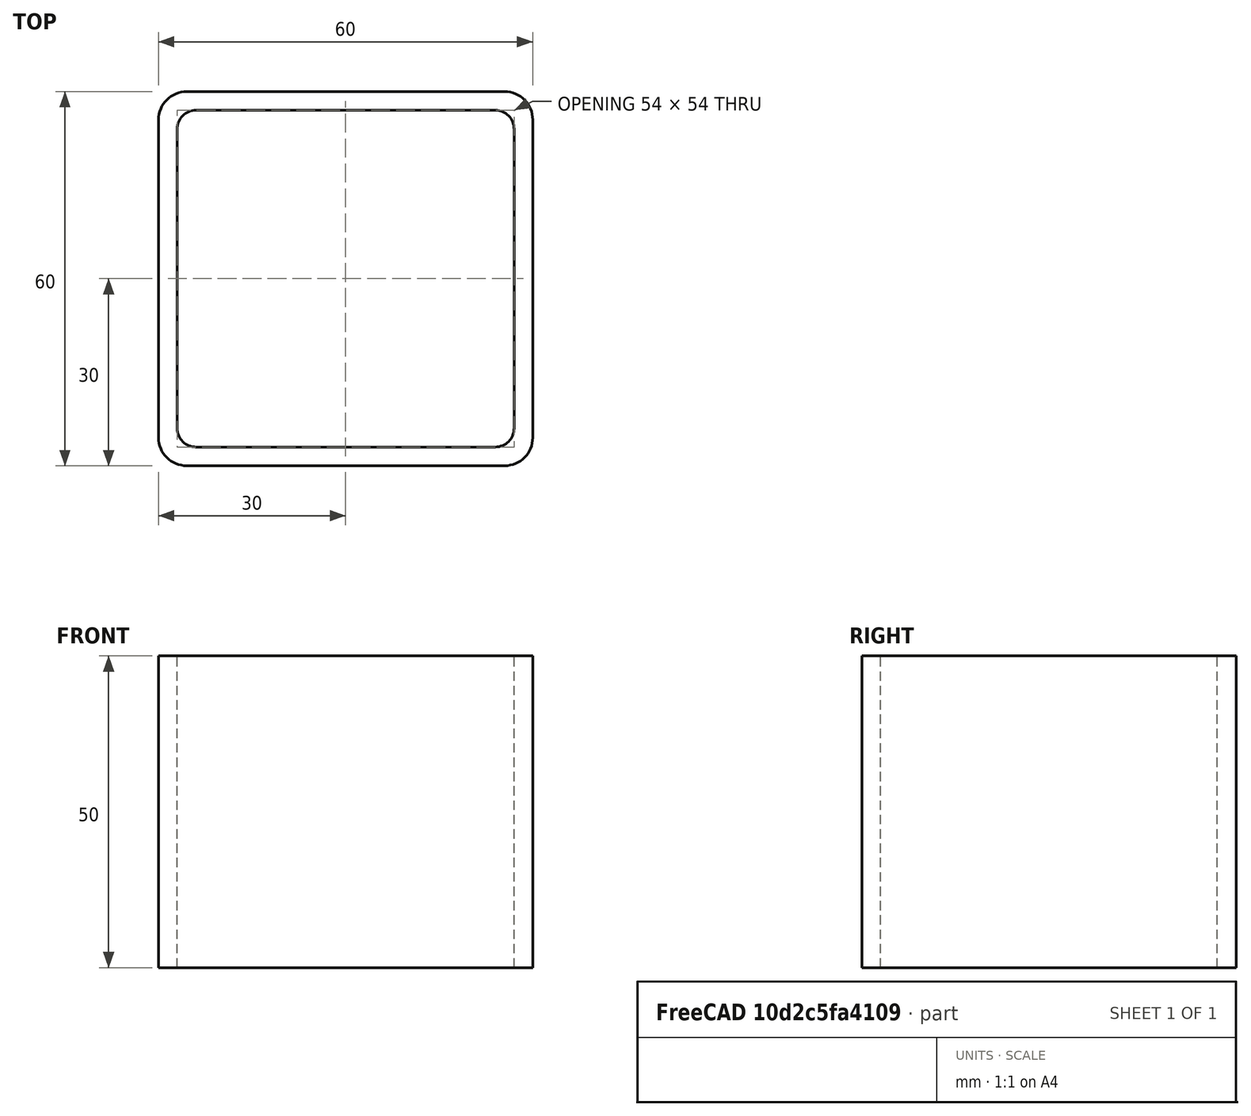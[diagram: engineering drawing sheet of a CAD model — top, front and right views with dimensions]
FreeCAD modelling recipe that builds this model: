
FCSTD DOCUMENT  (FreeCAD 0.15R4671 (Git))
Label: Square hollow section 60x60x3 EN10219 S235JRH
License: All rights reserved
LicenseURL: http://en.wikipedia.org/wiki/All_rights_reserved
objects: Sketcher::SketchObject×1, Part::Extrusion×1
note: 2 computed .brp shape members not serialized (recipe doc carries the construction recipe); baked Part::Feature solids carry a one-line shape summary decoded from their .brp

FEATURE [Sketcher::SketchObject] Sketch
  sketch-geometry (16):
    g0: LineSegment StartX=-24 StartY=27 StartZ=0 EndX=24 EndY=27 EndZ=0
    g1: LineSegment StartX=27 StartY=24 StartZ=0 EndX=27 EndY=-24 EndZ=0
    g2: LineSegment StartX=24 StartY=-27 StartZ=0 EndX=-24 EndY=-27 EndZ=0
    g3: LineSegment StartX=-27 StartY=-24 StartZ=0 EndX=-27 EndY=24 EndZ=0
    g4: LineSegment StartX=-25.5 StartY=30 StartZ=0 EndX=25.5 EndY=30 EndZ=0
    g5: LineSegment StartX=30 StartY=25.5 StartZ=0 EndX=30 EndY=-25.5 EndZ=0
    g6: LineSegment StartX=25.5 StartY=-30 StartZ=0 EndX=-25.5 EndY=-30 EndZ=0
    g7: LineSegment StartX=-30 StartY=-25.5 StartZ=0 EndX=-30 EndY=25.5 EndZ=0
    g8: ArcOfCircle CenterX=-24 CenterY=24 CenterZ=0 NormalX=0 NormalY=0 NormalZ=1 Radius=3 StartAngle=1.5708 EndAngle=3.14159
    g9: ArcOfCircle CenterX=24 CenterY=24 CenterZ=0 NormalX=0 NormalY=0 NormalZ=1 Radius=3 StartAngle=0 EndAngle=1.5708
    g10: ArcOfCircle CenterX=24 CenterY=-24 CenterZ=0 NormalX=0 NormalY=0 NormalZ=1 Radius=3 StartAngle=4.71239 EndAngle=6.28319
    g11: ArcOfCircle CenterX=-24 CenterY=-24 CenterZ=0 NormalX=0 NormalY=0 NormalZ=1 Radius=3 StartAngle=3.14159 EndAngle=4.71239
    g12: ArcOfCircle CenterX=25.5 CenterY=25.5 CenterZ=0 NormalX=0 NormalY=0 NormalZ=1 Radius=4.5 StartAngle=0 EndAngle=1.5708
    g13: ArcOfCircle CenterX=25.5 CenterY=-25.5 CenterZ=0 NormalX=0 NormalY=0 NormalZ=1 Radius=4.5 StartAngle=4.71239 EndAngle=6.28319
    g14: ArcOfCircle CenterX=-25.5 CenterY=-25.5 CenterZ=0 NormalX=0 NormalY=0 NormalZ=1 Radius=4.5 StartAngle=3.14159 EndAngle=4.71239
    g15: ArcOfCircle CenterX=-25.5 CenterY=25.5 CenterZ=0 NormalX=0 NormalY=0 NormalZ=1 Radius=4.5 StartAngle=1.5708 EndAngle=3.14159
  constraints (36):
    c: Horizontal(g2)
    c: Vertical(g3)
    c: Horizontal(g6)
    c: Vertical(g7)
    c: Tangent(g3,g8) = 1.5708
    c: Tangent(g0,g8) = 1.5708
    c: Tangent(g0,g9) = 1.5708
    c: Tangent(g1,g9) = 1.5708
    c: Tangent(g1,g10) = 1.5708
    c: Tangent(g2,g10) = 1.5708
    c: Tangent(g2,g11) = 1.5708
    c: Tangent(g3,g11) = 1.5708
    c: Tangent(g4,g12) = 1.5708
    c: Tangent(g5,g12) = 1.5708
    c: Tangent(g5,g13) = 1.5708
    c: Tangent(g6,g13) = 1.5708
    c: Tangent(g6,g14) = 1.5708
    c: Tangent(g7,g14) = 1.5708
    c: Tangent(g7,g15) = 1.5708
    c: Tangent(g4,g15) = 1.5708
    c: Equal(g9,g8)
    c: Equal(g9,g11)
    c: Equal(g9,g10)
    c: Equal(g12,g15)
    c: Equal(g12,g14)
    c: Equal(g12,g13)
    c: Symmetric(g4,g6,g-1)
    c: Symmetric(g7,g5,g-2)
    c: DistanceY(g4,g6) = -60
    c: DistanceX(g7,g5) = 60
    c: Symmetric(g3,g1,g-2)
    c: Symmetric(g0,g2,g-1)
    c: DistanceY(g0,g4) = 3
    c: DistanceX(g5,g1) = -3
    c: Radius(g9) = 3
    c: Radius(g12) = 4.5
FEATURE [Part::Extrusion] Extrude  label="Square hollow section 60x60x3 EN10219 S235JRH"
  Base = -> Sketch
  Dir = (0,0,50)
  Solid = true
